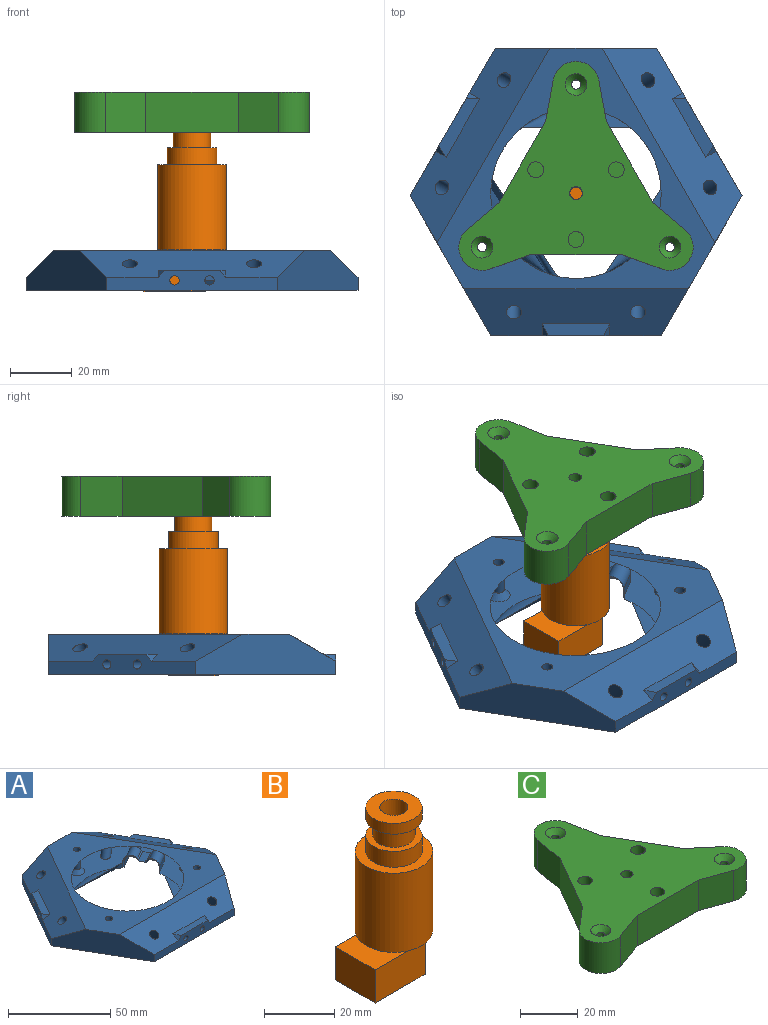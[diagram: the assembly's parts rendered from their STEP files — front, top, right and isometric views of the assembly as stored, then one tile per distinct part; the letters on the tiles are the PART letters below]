
ASSEMBLY  parts=3 mates=2
PART A: 76 faces, bbox 217.2x202.8x125.5 mm
  f0: plane 107.17x92.82mm, normal (0,0,-1), area 4340.9mm2, adj f3,f4,f5,f6,f8,f9,f10,f14
  f1: plane 72.56x15.21mm, normal (0,-0.5,0.87), area 985.5mm2, adj f2,f3,f4,f5,f8,f9,f22,f25
  f2: plane 199.61x187.61mm, normal (0,0,1), area 2143.8mm2, adj f1,f3,f5,f7,f27,f29,f49,f70
  f3: plane 45.18x26.09mm, normal (-0.87,-0.5,0), area 524mm2, adj f0,f1,f2,f4,f49,f50
  f4: plane 55x6.45mm, normal (0,-1,0), area 262mm2, adj f0,f1,f3,f5,f22,f23,f24,f25
  f5: plane 45.18x26.09mm, normal (0.87,-0.5,0), area 524mm2, adj f0,f1,f2,f4,f27,f28
  f6: cylinder r=27.5mm len=55mm, axis (0,0,-1), area 68mm2, adj f0,f12,f17,f18,f20,f21,f34,f39
  f7: cylinder r=27.5mm len=50.91mm, axis (0,0,-1), area 0mm2, adj f2
  f8: cylinder r=2.45mm len=12.3mm, axis (0,-0.5,0.87), area 153mm2, adj f0,f1
  f9: cylinder r=2.45mm len=12.3mm, axis (0,-0.5,0.87), area 153mm2, adj f0,f1
  f10: plane 9.32x3.23mm, normal (-1,0,0), area 30.1mm2, adj f0,f11,f15,f21
  f11: cylinder r=3.23mm len=9.32mm, axis (0,1,0), area 72.8mm2, adj f10,f15,f19,f20
  f12: plane 8.55x3.94mm, normal (0,0,-1), area 33.4mm2, adj f6,f15,f16,f17,f19,f20
  f13: cylinder r=3.23mm len=9.32mm, axis (0,1,0), area 72.8mm2, adj f14,f15,f16,f17
  f14: plane 9.32x3.23mm, normal (1,0,0), area 30.1mm2, adj f0,f13,f15,f18
  f15: plane 17.73x6.45mm, normal (0,1,0), area 80.9mm2, adj f0,f10,f11,f12,f13,f14,f16,f19
  f16: plane 8.28x0.91mm, normal (-0.52,0,-0.86), area 7.5mm2, adj f12,f13,f15,f17
  f17: bspline ~8x4.19mm, area 12.8mm2, adj f6,f12,f13,f16,f18
  f18: plane 3.23x0.86mm, normal (0.82,0.57,0), area 3.4mm2, adj f0,f6,f14,f17
  f19: plane 8.28x0.91mm, normal (0.52,0,-0.86), area 7.5mm2, adj f11,f12,f15,f20
  f20: bspline ~8x4.19mm, area 12.8mm2, adj f6,f11,f12,f19,f21
  f21: plane 3.23x0.86mm, normal (-0.82,0.57,0), area 3.4mm2, adj f0,f6,f10,f20
  f22: plane 21.73x3.87mm, normal (0,0,1), area 76.5mm2, adj f1,f4,f25,f26
  f23: cylinder r=1.5mm len=10mm, axis (0,1,0), area 94.2mm2, adj f4,f15
  f24: cylinder r=1.5mm len=10mm, axis (0,1,0), area 94.2mm2, adj f4,f15
  f25: plane 3.87x2.23mm, normal (-0.71,-0.35,0.61), area 6.1mm2, adj f1,f4,f22
  f26: plane 3.87x2.23mm, normal (0.71,-0.35,0.61), area 6.1mm2, adj f1,f4,f22
  f27: plane 62.84x45.06mm, normal (0.43,0.25,0.87), area 985.5mm2, adj f2,f5,f28,f29,f30,f31,f44,f47
  f28: plane 47.63x27.5mm, normal (0.87,0.5,0), area 262mm2, adj f0,f5,f27,f29,f44,f45,f46,f47
  f29: plane 52.17x13mm, normal (0,1,0), area 524mm2, adj f0,f2,f27,f28,f49,f50
  f30: cylinder r=2.45mm len=12.3mm, axis (0.43,0.25,0.87), area 153mm2, adj f0,f27
  f31: cylinder r=2.45mm len=12.3mm, axis (0.43,0.25,0.87), area 153mm2, adj f0,f27
  f32: plane 8.07x4.66mm, normal (0.5,-0.87,0), area 30.1mm2, adj f0,f33,f37,f43
  f33: cylinder r=3.23mm len=11.11mm, axis (-0.87,-0.5,0), area 72.8mm2, adj f32,f37,f41,f42
  f34: plane 9.17x7.51mm, normal (0,0,-1), area 33.4mm2, adj f6,f37,f38,f39,f41,f42
  f35: cylinder r=3.23mm len=11.11mm, axis (-0.87,-0.5,0), area 72.8mm2, adj f36,f37,f38,f39
  f36: plane 8.07x4.66mm, normal (-0.5,0.87,0), area 30.1mm2, adj f0,f35,f37,f40
  f37: plane 15.35x8.86mm, normal (-0.87,-0.5,0), area 80.9mm2, adj f0,f32,f33,f34,f35,f36,f38,f41
  f38: plane 7.59x4.63mm, normal (0.26,-0.45,-0.86), area 7.5mm2, adj f34,f35,f37,f39
  f39: bspline ~7.75x4.19mm, area 12.8mm2, adj f6,f34,f35,f38,f40
  f40: plane 113.23x110.95mm, normal (-0.91,0.42,0), area 3.4mm2, adj f0,f6,f36,f39
  f41: plane 7.18x4.89mm, normal (-0.26,0.45,-0.86), area 7.5mm2, adj f33,f34,f37,f42
  f42: bspline ~6.11x5.73mm, area 12.8mm2, adj f6,f33,f34,f41,f43
  f43: plane 3.23x1.04mm, normal (-0.09,-1,0), area 3.4mm2, adj f0,f6,f32,f42
  f44: plane 19.08x13.25mm, normal (0,0,1), area 76.5mm2, adj f27,f28,f47,f48
  f45: cylinder r=1.5mm len=10.16mm, axis (-0.87,-0.5,0), area 94.2mm2, adj f28,f37
  f46: cylinder r=1.5mm len=10.16mm, axis (-0.87,-0.5,0), area 94.2mm2, adj f28,f37
  f47: plane 3.61x3.35mm, normal (0.66,-0.44,0.61), area 6.1mm2, adj f27,f28,f44
  f48: plane 4.31x2.23mm, normal (-0.05,0.79,0.61), area 6.1mm2, adj f27,f28,f44
  f49: plane 62.84x45.06mm, normal (-0.43,0.25,0.87), area 985.5mm2, adj f2,f3,f29,f50,f51,f52,f65,f68
  f50: plane 47.63x27.5mm, normal (-0.87,0.5,0), area 262mm2, adj f0,f3,f29,f49,f65,f66,f67,f68
  f51: cylinder r=2.45mm len=12.3mm, axis (-0.43,0.25,0.87), area 153mm2, adj f0,f49
  f52: cylinder r=2.45mm len=12.3mm, axis (-0.43,0.25,0.87), area 153mm2, adj f0,f49
  f53: plane 8.07x4.66mm, normal (0.5,0.87,0), area 30.1mm2, adj f0,f54,f58,f64
  f54: cylinder r=3.23mm len=11.11mm, axis (0.87,-0.5,0), area 72.8mm2, adj f53,f58,f62,f63
  f55: plane 9.17x7.51mm, normal (0,0,-1), area 33.4mm2, adj f6,f58,f59,f60,f62,f63
  f56: cylinder r=3.23mm len=11.11mm, axis (0.87,-0.5,0), area 72.8mm2, adj f57,f58,f59,f60
  f57: plane 8.07x4.66mm, normal (-0.5,-0.87,0), area 30.1mm2, adj f0,f56,f58,f61
  f58: plane 15.35x8.86mm, normal (0.87,-0.5,0), area 80.9mm2, adj f0,f53,f54,f55,f56,f57,f59,f62
  f59: plane 7.18x4.89mm, normal (0.26,0.45,-0.86), area 7.5mm2, adj f55,f56,f58,f60
  f60: bspline ~6.11x5.73mm, area 12.8mm2, adj f6,f55,f56,f59,f61
  f61: plane 3.23x1.04mm, normal (0.09,-1,0), area 3.4mm2, adj f0,f6,f57,f60
  f62: plane 7.59x4.63mm, normal (-0.26,-0.45,-0.86), area 7.5mm2, adj f54,f55,f58,f63
  f63: bspline ~7.75x4.19mm, area 12.8mm2, adj f6,f54,f55,f62,f64
  f64: plane 3.23x0.95mm, normal (0.91,0.42,0), area 3.4mm2, adj f0,f6,f53,f63
  f65: plane 19.08x13.25mm, normal (0,0,1), area 76.5mm2, adj f49,f50,f68,f69
  f66: cylinder r=1.5mm len=10.16mm, axis (0.87,-0.5,0), area 94.2mm2, adj f50,f58
  f67: cylinder r=1.5mm len=10.16mm, axis (0.87,-0.5,0), area 94.2mm2, adj f50,f58
  f68: plane 4.31x2.23mm, normal (0.05,0.79,0.61), area 6.1mm2, adj f49,f50,f65
  f69: plane 3.61x3.35mm, normal (-0.66,-0.44,0.61), area 6.1mm2, adj f49,f50,f65
  f70: cylinder r=1.75mm len=11mm, axis (0,0,1), area 121mm2, adj f2,f74
  f71: cylinder r=1.75mm len=11mm, axis (0,0,1), area 121mm2, adj f2,f75
  f72: cylinder r=1.75mm len=11mm, axis (0,0,1), area 121mm2, adj f2,f73
  f73: cone r=1.75mm half-angle=45deg, axis (0,0,-1), area 48.9mm2, adj f0,f72
  f74: cone r=1.75mm half-angle=45deg, axis (0,0,-1), area 48.9mm2, adj f0,f70
  f75: cone r=1.75mm half-angle=45deg, axis (0,0,-1), area 48.9mm2, adj f0,f71
PART B: 20 faces, bbox 26.5x22x56.3 mm
  f0: plane 16x16mm, normal (0,0,1), area 150.8mm2, adj f1,f13
  f1: cylinder r=4mm len=8mm, axis (0,0,1), area 163.4mm2, adj f0,f2
  f2: cone r=4mm half-angle=45deg, axis (0,0,1), area 53.3mm2, adj f1,f3
  f3: cylinder r=2mm len=36.3mm, axis (0,0,1), area 456.2mm2, adj f2,f14
  f4: plane 20x16mm, normal (0,0,1), area 296.2mm2, adj f5,f15,f16,f17,f18
  f5: cylinder r=2.75mm len=5.5mm, axis (0,0,1), area 36.3mm2, adj f4,f6
  f6: plane 22x22mm, normal (0,0,-1), area 356.4mm2, adj f5,f7
  f7: cylinder r=11mm len=27.5mm, axis (0,0,1), area 1900.7mm2, adj f6,f8
  f8: plane 22x22mm, normal (0,0,1), area 179.1mm2, adj f7,f9
  f9: cylinder r=8mm len=16mm, axis (0,0,1), area 276.5mm2, adj f8,f10
  f10: plane 16x16mm, normal (0,0,1), area 88mm2, adj f9,f11
  f11: cylinder r=6mm len=12mm, axis (0,0,1), area 226.2mm2, adj f10,f12
  f12: plane 16x16mm, normal (0,0,-1), area 88mm2, adj f11,f13
  f13: cylinder r=8mm len=16mm, axis (0,0,1), area 186mm2, adj f0,f12
  f14: plane 4x4mm, normal (0,0,1), area 12.6mm2, adj f3
  f15: plane 16x11.5mm, normal (-1,0,0), area 184mm2, adj f4,f16,f18,f19
  f16: plane 20x11.5mm, normal (0,-1,0), area 230mm2, adj f4,f15,f17,f19
  f17: plane 16x11.5mm, normal (1,0,0), area 184mm2, adj f4,f16,f18,f19
  f18: plane 20x11.5mm, normal (0,1,0), area 230mm2, adj f4,f15,f17,f19
  f19: plane 20x16mm, normal (0,0,-1), area 320mm2, adj f15,f16,f17,f18
PART C: 40 faces, bbox 75.6x67.5x13 mm
  f0: plane 75.62x67.5mm, normal (0,0,-1), area 2153.7mm2, adj f1,f3,f4,f5,f6,f7,f15,f17
  f1: plane 25.98x15mm, normal (-0.87,0.5,0), area 390mm2, adj f0,f6,f12,f18
  f2: cylinder r=8.15mm len=16.3mm, axis (0,0,-1), area 220.2mm2, adj f8,f33
  f3: plane 25.98x15mm, normal (0.87,0.5,0), area 390mm2, adj f0,f4,f12,f27
  f4: plane 13.36x13mm, normal (0.98,0.18,0), area 176.5mm2, adj f0,f3,f5,f12
  f5: cylinder r=7.5mm len=14.76mm, axis (0,0,-1), area 271mm2, adj f0,f4,f6,f12
  f6: plane 13.36x13mm, normal (-0.98,0.18,0), area 176.5mm2, adj f0,f1,f5,f12
  f7: cylinder r=1.5mm len=11mm, axis (0,0,-1), area 103.7mm2, adj f0,f16
  f8: plane 16.3x16.3mm, normal (0,0,-1), area 151.9mm2, adj f2,f32
  f9: cylinder r=3.75mm len=7.5mm, axis (0,0,-1), area 58.9mm2, adj f10,f32
  f10: plane 7.5x7.5mm, normal (0,0,-1), area 22.9mm2, adj f9,f31
  f11: cylinder r=2.1mm len=4.7mm, axis (0,0,-1), area 62mm2, adj f12,f31
  f12: plane 75.62x67.5mm, normal (0,0,1), area 2280.7mm2, adj f1,f3,f4,f5,f6,f11,f13,f14
  f13: cylinder r=2.55mm len=10mm, axis (0,0,-1), area 160.2mm2, adj f12,f39
  f14: cylinder r=2.55mm len=10mm, axis (0,0,-1), area 160.2mm2, adj f12,f38
  f15: cylinder r=2.55mm len=10mm, axis (0,0,-1), area 160.2mm2, adj f0,f36
  f16: cone r=1.5mm half-angle=45deg, axis (0,0,1), area 44.4mm2, adj f7,f12
  f17: plane 30x13mm, normal (0,-1,0), area 390mm2, adj f0,f12,f20,f25
  f18: plane 13x10.35mm, normal (-0.65,0.76,0), area 176.5mm2, adj f0,f1,f12,f19
  f19: cylinder r=7.5mm len=13.21mm, axis (0,0,-1), area 271mm2, adj f0,f12,f18,f20
  f20: plane 13x12.79mm, normal (0.34,-0.94,0), area 176.5mm2, adj f0,f12,f17,f19
  f21: cylinder r=1.5mm len=11mm, axis (0,0,-1), area 103.7mm2, adj f0,f24
  f22: cylinder r=2.55mm len=10mm, axis (0,0,-1), area 160.2mm2, adj f12,f37
  f23: cylinder r=2.55mm len=10mm, axis (0,0,-1), area 160.2mm2, adj f0,f35
  f24: cone r=1.5mm half-angle=45deg, axis (0,0,1), area 44.4mm2, adj f12,f21
  f25: plane 13x12.79mm, normal (-0.34,-0.94,0), area 176.5mm2, adj f0,f12,f17,f26
  f26: cylinder r=7.5mm len=13.21mm, axis (0,0,-1), area 271mm2, adj f0,f12,f25,f27
  f27: plane 13x10.35mm, normal (0.65,0.76,0), area 176.5mm2, adj f0,f3,f12,f26
  f28: cylinder r=1.5mm len=11mm, axis (0,0,-1), area 103.7mm2, adj f0,f30
  f29: cylinder r=2.55mm len=10mm, axis (0,0,-1), area 160.2mm2, adj f0,f34
  f30: cone r=1.5mm half-angle=45deg, axis (0,0,1), area 44.4mm2, adj f12,f28
  f31: cone r=2.1mm half-angle=45deg, axis (0,0,-1), area 10.4mm2, adj f10,f11
  f32: cone r=3.75mm half-angle=45deg, axis (0,0,-1), area 17.8mm2, adj f8,f9
  f33: cone r=8.15mm half-angle=45deg, axis (0,0,-1), area 37.3mm2, adj f0,f2
  f34: plane 5.1x5.1mm, normal (0,0,-1), area 20.4mm2, adj f29
  f35: plane 5.1x5.1mm, normal (0,0,-1), area 20.4mm2, adj f23
  f36: plane 5.1x5.1mm, normal (0,0,-1), area 20.4mm2, adj f15
  f37: plane 5.1x5.1mm, normal (0,0,1), area 20.4mm2, adj f22
  f38: plane 5.1x5.1mm, normal (0,0,1), area 20.4mm2, adj f14
  f39: plane 5.1x5.1mm, normal (0,0,1), area 20.4mm2, adj f13
PLACE A at identity
PLACE B t=(0,0,47.8)mm
PLACE C t=(0,0,43)mm
MATE fastened B.f1 <-> C.f9  axis (0,0,1) through (0,0,47.8)mm
MATE fastened C.f2 <-> A.f6  axis (0,0,-1) through (0,0,43)mm
